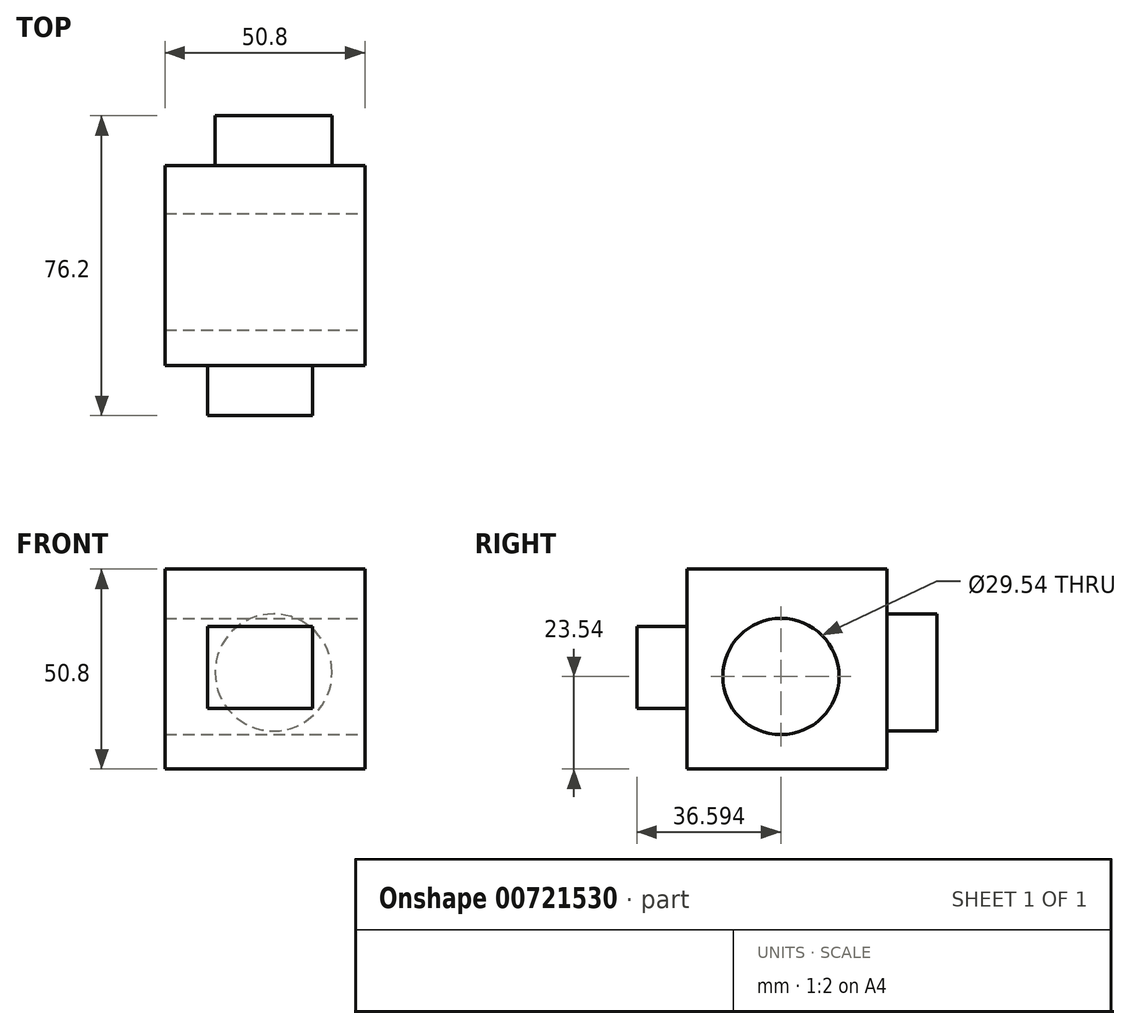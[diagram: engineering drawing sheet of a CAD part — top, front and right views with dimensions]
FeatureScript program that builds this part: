
annotation { "Feature Type Name" : "Feature", "Feature Type Description" : "" }
export const myFeature = defineFeature(function(context is Context, id is Id, definition is map)
    precondition{}
    {
        {
            var Q0;
            Q0=qCreatedBy(makeId("Front.planeOp"),FACE);
            var sketch = newSketch(context, id + "F0", { "sketchPlane" : qUnion([Q0])});
            skLineSegment(sketch, "E0", {"start": v(-56.15, 55.38) * mm, "end": v(-56.15, 4.58) * mm});
            skLineSegment(sketch, "E1", {"start": v(-56.15, 4.58) * mm, "end": v(-5.35, 4.58) * mm});
            skLineSegment(sketch, "E2", {"start": v(-5.35, 4.58) * mm, "end": v(-5.35, 55.38) * mm});
            skLineSegment(sketch, "E3", {"start": v(-5.35, 55.38) * mm, "end": v(-56.15, 55.38) * mm});
            skSolve(sketch);
        }
        {
            var Q0;
            Q0 = qSketchRegion(id + "F0", true);
            extrude(context, id + "F1", {"entities" : qUnion([Q0]), "depth" : 50.8 * mm, "offsetDistance" : 25.4 * mm});
        }
        {
            var Q0;
            Q0=makeQuery(id+"F1.opExtrude","SWEPT_FACE",FACE,{"disambiguationData":[OSD([sQuery(id+"F0.wireOp",EDGE,"E2")])]});
            var sketch = newSketch(context, id + "F2", { "sketchPlane" : qUnion([Q0])});
            skCircle(sketch, "E4", {"center": v(-26.9, 28.12) * mm, "radius": 14.77 * mm});
            skSolve(sketch);
        }
        {
            var Q0;
            Q0=makeQuery(id+"F2.imprint","IMPRINT",FACE,{"disambiguationData":[TD([[makeQuery(id+"F2.imprint","IMPRINT",EDGE,{"derivedFrom":sQuery(id+"F2.wireOp",EDGE,"E4")}),1.0]])]});
            extrude(context, id + "F3", {"entities" : qUnion([Q0]), "operationType" : NewBodyOperationType.REMOVE, "oppositeDirection" : true, "depth" : 50.8 * mm, "offsetDistance" : 25.4 * mm});
        }
        {
            var Q0;
            Q0=makeQuery(id+"F1.opExtrude","CAP_FACE",FACE,{"disambiguationData":[OSD([sQuery(id+"F0.wireOp",EDGE,"E0"),sQuery(id+"F0.wireOp",EDGE,"E1"),sQuery(id+"F0.wireOp",EDGE,"E2"),sQuery(id+"F0.wireOp",EDGE,"E3")])],"isStart":true});
            var sketch = newSketch(context, id + "F4", { "sketchPlane" : qUnion([Q0])});
            skCircle(sketch, "E5", {"center": v(28.52, 29.13) * mm, "radius": 14.86 * mm});
            skSolve(sketch);
        }
        {
            var Q0;
            Q0=makeQuery(id+"F4.imprint","IMPRINT",FACE,{"disambiguationData":[TD([[makeQuery(id+"F4.imprint","IMPRINT",EDGE,{"derivedFrom":sQuery(id+"F4.wireOp",EDGE,"E5")}),1.0]])]});
            extrude(context, id + "F5", {"entities" : qUnion([Q0]), "operationType" : NewBodyOperationType.ADD, "depth" : 12.7 * mm, "offsetDistance" : 25.4 * mm});
        }
        {
            var Q0;
            Q0=makeQuery(id+"F1.opExtrude","CAP_FACE",FACE,{"disambiguationData":[OSD([sQuery(id+"F0.wireOp",EDGE,"E0"),sQuery(id+"F0.wireOp",EDGE,"E1"),sQuery(id+"F0.wireOp",EDGE,"E2"),sQuery(id+"F0.wireOp",EDGE,"E3")])],"isStart":false});
            var sketch = newSketch(context, id + "F6", { "sketchPlane" : qUnion([Q0])});
            skLineSegment(sketch, "E6.bottom", {"start": v(-45.32, 40.86) * mm, "end": v(-18.61, 40.86) * mm});
            skLineSegment(sketch, "E6.top", {"start": v(-45.32, 20.03) * mm, "end": v(-18.61, 20.03) * mm});
            skLineSegment(sketch, "E6.left", {"start": v(-45.32, 40.86) * mm, "end": v(-45.32, 20.03) * mm});
            skLineSegment(sketch, "E6.right", {"start": v(-18.61, 40.86) * mm, "end": v(-18.61, 20.03) * mm});
            skSolve(sketch);
        }
        {
            var Q0;
            Q0=makeQuery(id+"F6.imprint","IMPRINT",FACE,{"disambiguationData":[TD([[makeQuery(id+"F6.imprint","IMPRINT",EDGE,{"derivedFrom":sQuery(id+"F6.wireOp",EDGE,"E6.bottom")}),-1.0]])]});
            extrude(context, id + "F7", {"entities" : qUnion([Q0]), "operationType" : NewBodyOperationType.ADD, "depth" : 12.7 * mm, "offsetDistance" : 25.4 * mm});
        }
    });
